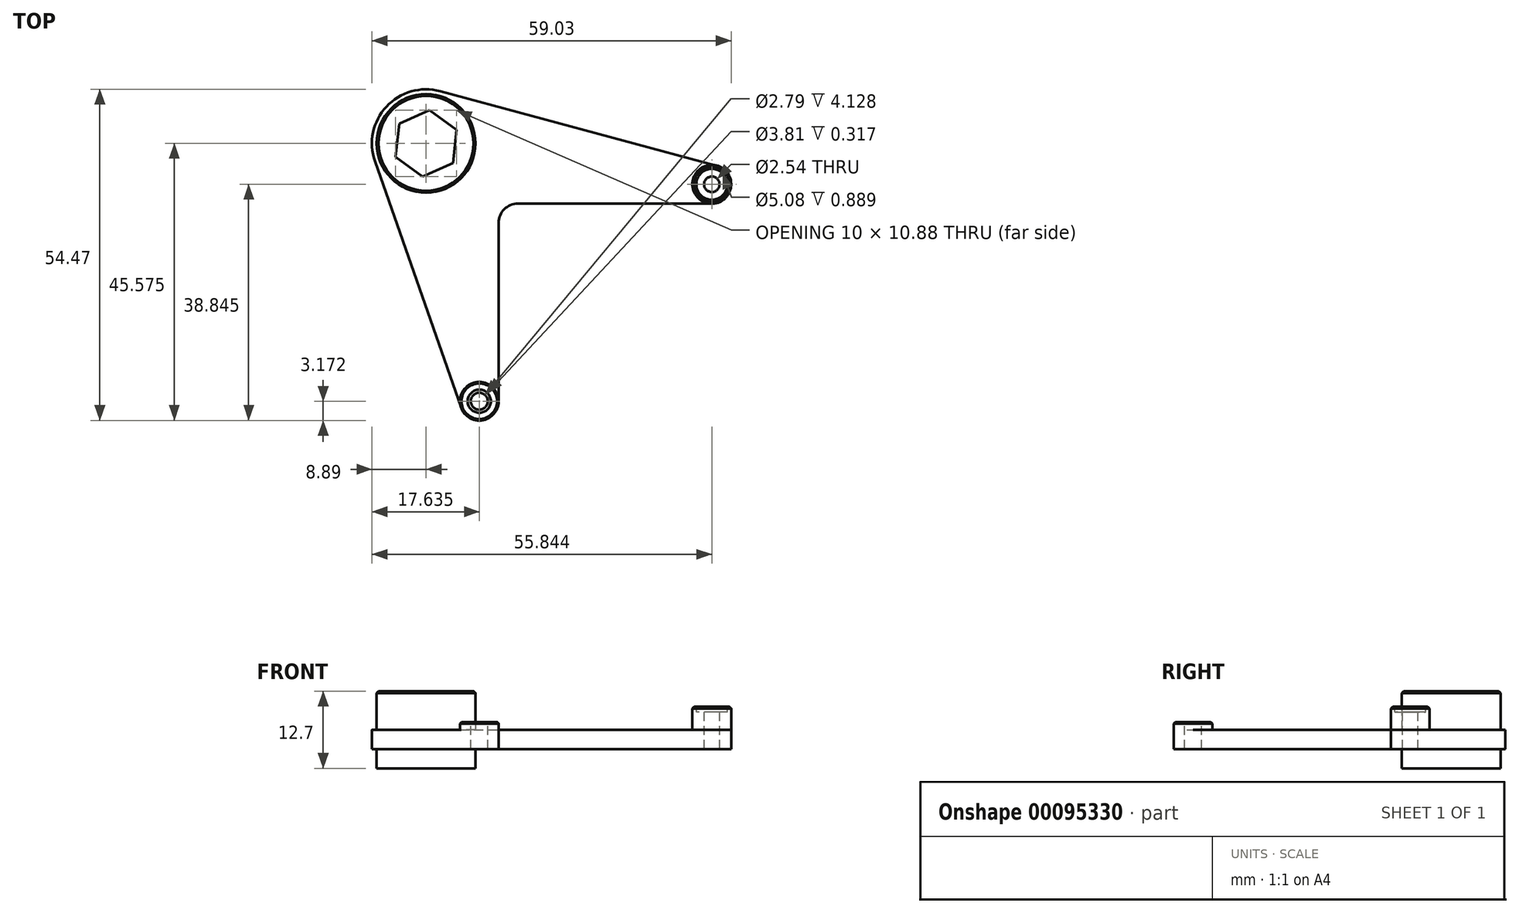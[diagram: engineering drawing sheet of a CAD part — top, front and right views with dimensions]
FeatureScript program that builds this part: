
annotation { "Feature Type Name" : "Feature", "Feature Type Description" : "" }
export const myFeature = defineFeature(function(context is Context, id is Id, definition is map)
    precondition{}
    {
        {
            var Q0;
            Q0=qCreatedBy(makeId("Top.planeOp"),FACE);
            var sketch = newSketch(context, id + "F0", { "sketchPlane" : qUnion([Q0])});
            skLineSegment(sketch, "E0", {"start": v(59.03, 0) * mm, "end": v(0, 0) * mm});
            skLineSegment(sketch, "E1", {"start": v(0, 0) * mm, "end": v(0, -51.23) * mm});
            skLineSegment(sketch, "E2", {"start": v(0, -51.23) * mm, "end": v(-25.86, 22.87) * mm});
            skLineSegment(sketch, "E3", {"start": v(-25.86, 22.87) * mm, "end": v(59.03, 0) * mm});
            skSolve(sketch);
        }
        {
            var Q0;
            Q0 = qSketchRegion(id + "F0", true);
            extrude(context, id + "F1", {"entities" : qUnion([Q0]), "endBound" : BoundingType.SYMMETRIC, "depth" : 3.17 * mm});
        }
        {
            var Q0;
            Q0=makeQuery(id+"F1.opExtrude","SWEPT_EDGE",EDGE,{"disambiguationData":[OSD([sQuery(id+"F0.wireOp",EDGE,"E2"),sQuery(id+"F0.wireOp",EDGE,"E3")])]});
            fillet(context, id + "F2", {"entities" : qUnion([Q0]), "radius" : 8.9 * mm, "tangentPropagation" : true, "allowEdgeOverflow" : false});
        }
        {
            var Q0;
            Q0=makeQuery(id+"F1.opExtrude","SWEPT_EDGE",EDGE,{"disambiguationData":[OSD([sQuery(id+"F0.wireOp",EDGE,"E0"),sQuery(id+"F0.wireOp",EDGE,"E3")])]});
            var Q1;
            Q1=makeQuery(id+"F1.opExtrude","SWEPT_EDGE",EDGE,{"disambiguationData":[OSD([sQuery(id+"F0.wireOp",EDGE,"E1"),sQuery(id+"F0.wireOp",EDGE,"E2")])]});
            var Q2;
            Q2=makeQuery(id+"F1.opExtrude","SWEPT_EDGE",EDGE,{"disambiguationData":[OSD([sQuery(id+"F0.wireOp",EDGE,"E0"),sQuery(id+"F0.wireOp",EDGE,"E1")])]});
            fillet(context, id + "F3", {"entities" : qUnion([Q0, Q1, Q2]), "radius" : 3.17 * mm, "tangentPropagation" : true, "allowEdgeOverflow" : false});
        }
        {
            var Q0;
            Q0=makeQuery(id+"F1.opExtrude","CAP_FACE",FACE,{"disambiguationData":[OSD([sQuery(id+"F0.wireOp",EDGE,"E0"),sQuery(id+"F0.wireOp",EDGE,"E1"),sQuery(id+"F0.wireOp",EDGE,"E2"),sQuery(id+"F0.wireOp",EDGE,"E3")])],"isStart":false});
            var sketch = newSketch(context, id + "F4", { "sketchPlane" : qUnion([Q0])});
            skCircle(sketch, "E4", {"center": v(-3.18, -32.5) * mm, "radius": 3.17 * mm});
            skSolve(sketch);
        }
        {
            var Q0;
            Q0 = qSketchRegion(id + "F4", true);
            extrude(context, id + "F5", {"entities" : qUnion([Q0]), "operationType" : NewBodyOperationType.ADD, "depth" : 1.27 * mm});
        }
        {
            var Q0;
            Q0=makeQuery(id+"F1.opExtrude","CAP_FACE",FACE,{"disambiguationData":[OSD([sQuery(id+"F0.wireOp",EDGE,"E0"),sQuery(id+"F0.wireOp",EDGE,"E1"),sQuery(id+"F0.wireOp",EDGE,"E2"),sQuery(id+"F0.wireOp",EDGE,"E3")])],"isStart":false});
            var sketch = newSketch(context, id + "F6", { "sketchPlane" : qUnion([Q0])});
            skCircle(sketch, "E5", {"center": v(35.03, 3.17) * mm, "radius": 3.19 * mm});
            skSolve(sketch);
        }
        {
            var Q0;
            Q0 = qSketchRegion(id + "F6", true);
            extrude(context, id + "F7", {"entities" : qUnion([Q0]), "operationType" : NewBodyOperationType.ADD, "depth" : 3.8 * mm});
        }
        {
            var Q0;
            Q0=makeQuery(id+"F1.opExtrude","CAP_FACE",FACE,{"disambiguationData":[OSD([sQuery(id+"F0.wireOp",EDGE,"E0"),sQuery(id+"F0.wireOp",EDGE,"E1"),sQuery(id+"F0.wireOp",EDGE,"E2"),sQuery(id+"F0.wireOp",EDGE,"E3")])],"isStart":false});
            var sketch = newSketch(context, id + "F8", { "sketchPlane" : qUnion([Q0])});
            skPoint(sketch, "E6.centerSnap0", {"position": v(-18.43, 15.96) * mm});
            skCircle(sketch, "E7", {"center": v(-11.92, 9.9) * mm, "radius": 8.12 * mm});
            skSolve(sketch);
        }
        {
            var Q0;
            Q0=makeQuery(id+"F8.imprint","IMPRINT",FACE,{"disambiguationData":[TD([[makeQuery(id+"F8.imprint","IMPRINT",EDGE,{"derivedFrom":sQuery(id+"F8.wireOp",EDGE,"E7")}),1.0]])]});
            extrude(context, id + "F9", {"entities" : qUnion([Q0]), "operationType" : NewBodyOperationType.ADD, "endBound" : BoundingType.SYMMETRIC, "depth" : 12.7 * mm});
        }
        {
            var Q0;
            Q0=makeQuery(id+"F9.opExtrude","CAP_FACE",FACE,{"disambiguationData":[OSD([sQuery(id+"F8.wireOp",EDGE,"E7")])],"isStart":false});
            var sketch = newSketch(context, id + "F10", { "sketchPlane" : qUnion([Q0])});
            skPoint(sketch, "E8", {"position": v(-11.92, 9.9) * mm});
            skCircle(sketch, "E9.cCircle", {"center": v(-11.92, 9.9) * mm, "radius": 4.74 * mm, "construction": true});
            skLineSegment(sketch, "E9.0", {"start": v(-11.34, 15.34) * mm, "end": v(-6.92, 12.12) * mm});
            skLineSegment(sketch, "E9.1", {"start": v(-6.92, 12.12) * mm, "end": v(-7.5, 6.68) * mm});
            skLineSegment(sketch, "E9.2", {"start": v(-7.5, 6.68) * mm, "end": v(-12.5, 4.47) * mm});
            skLineSegment(sketch, "E9.3", {"start": v(-12.5, 4.47) * mm, "end": v(-16.92, 7.69) * mm});
            skLineSegment(sketch, "E9.4", {"start": v(-16.92, 7.69) * mm, "end": v(-16.34, 13.13) * mm});
            skLineSegment(sketch, "E9.5", {"start": v(-16.34, 13.13) * mm, "end": v(-11.34, 15.34) * mm});
            skPoint(sketch, "E9.0.midPoint", {"position": v(-9.13, 13.73) * mm});
            skSolve(sketch);
        }
        {
            var Q0;
            Q0 = qSketchRegion(id + "F10", true);
            extrude(context, id + "F11", {"entities" : qUnion([Q0]), "operationType" : NewBodyOperationType.REMOVE, "endBound" : BoundingType.THROUGH_ALL, "oppositeDirection" : true, "depth" : 25.4 * mm});
        }
        {
            var Q0;
            Q0=makeQuery(id+"F5.opExtrude","CAP_FACE",FACE,{"disambiguationData":[OSD([sQuery(id+"F4.wireOp",EDGE,"E4")])],"isStart":false});
            var sketch = newSketch(context, id + "F12", { "sketchPlane" : qUnion([Q0])});
            skPoint(sketch, "E10", {"position": v(-3.18, -32.5) * mm});
            skSolve(sketch);
        }
        {
            var Q0;
            Q0=sQuery(id+"F12.wireOp",VERTEX,"E10");
            var Q1;
            Q1=makeQuery(id+"F1.opExtrude","SWEPT_BODY",BODY,{"disambiguationData":[OSD([sQuery(id+"F0.wireOp",EDGE,"E0"),sQuery(id+"F0.wireOp",EDGE,"E1"),sQuery(id+"F0.wireOp",EDGE,"E2"),sQuery(id+"F0.wireOp",EDGE,"E3")])]});
            hole(context, id + "F13", {"style" : HoleStyle.C_BORE, "endStyle" : HoleEndStyle.THROUGH, "holeDiameter" : 2.8 * mm, "cBoreDiameter" : 3.8 * mm, "cBoreDepth" : 0.32 * mm, "locations" : qUnion([Q0]), "scope" : qUnion([Q1]), "isTappedThrough" : true});
        }
        {
            var Q0;
            Q0=makeQuery(id+"F7.opExtrude","CAP_FACE",FACE,{"disambiguationData":[OSD([sQuery(id+"F6.wireOp",EDGE,"E5")])],"isStart":false});
            var sketch = newSketch(context, id + "F14", { "sketchPlane" : qUnion([Q0])});
            skPoint(sketch, "E11", {"position": v(35.03, 3.17) * mm});
            skSolve(sketch);
        }
        {
            var Q0;
            Q0=sQuery(id+"F14.wireOp",VERTEX,"E11");
            var Q1;
            Q1=makeQuery(id+"F1.opExtrude","SWEPT_BODY",BODY,{"disambiguationData":[OSD([sQuery(id+"F0.wireOp",EDGE,"E0"),sQuery(id+"F0.wireOp",EDGE,"E1"),sQuery(id+"F0.wireOp",EDGE,"E2"),sQuery(id+"F0.wireOp",EDGE,"E3")])]});
            hole(context, id + "F15", {"style" : HoleStyle.C_BORE, "endStyle" : HoleEndStyle.THROUGH, "holeDiameter" : 2.54 * mm, "cBoreDiameter" : 5.08 * mm, "cBoreDepth" : 0.89 * mm, "locations" : qUnion([Q0]), "scope" : qUnion([Q1]), "isTappedThrough" : true});
        }
        {
            var Q0;
            Q0=makeQuery(id+"F9.opExtrude","CAP_EDGE",EDGE,{"disambiguationData":[OSD([sQuery(id+"F8.wireOp",EDGE,"E7")])],"isStart":false});
            chamfer(context, id + "F16", {"entities" : qUnion([Q0]), "width" : 0.32 * mm, "tangentPropagation" : true});
        }
        {
            var Q0;
            Q0=makeQuery(id+"F5.opExtrude","CAP_EDGE",EDGE,{"disambiguationData":[OSD([sQuery(id+"F4.wireOp",EDGE,"E4")])],"isStart":false});
            chamfer(context, id + "F17", {"entities" : qUnion([Q0]), "width" : 0.25 * mm, "tangentPropagation" : true});
        }
        {
            var Q0;
            Q0=makeQuery(id+"F7.opExtrude","CAP_EDGE",EDGE,{"disambiguationData":[OSD([sQuery(id+"F6.wireOp",EDGE,"E5")])],"isStart":false});
            chamfer(context, id + "F18", {"entities" : qUnion([Q0]), "width" : 0.32 * mm, "tangentPropagation" : true});
        }
    });
